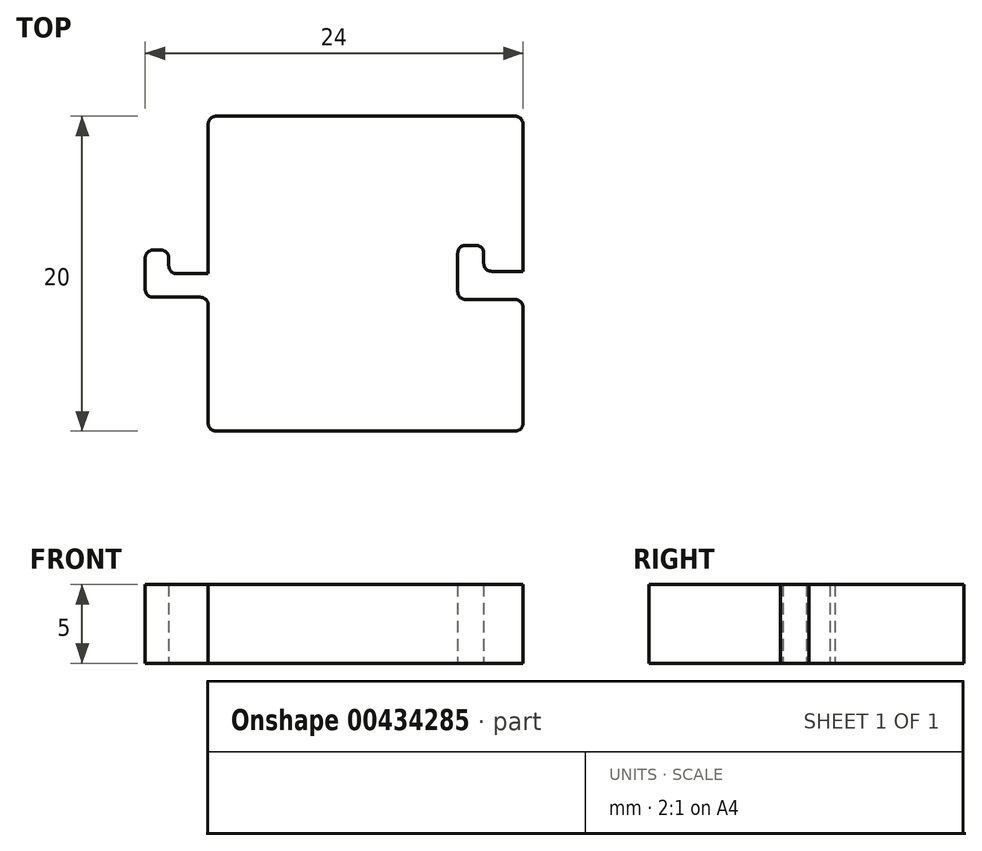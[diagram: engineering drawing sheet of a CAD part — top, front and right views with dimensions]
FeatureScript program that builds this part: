
annotation { "Feature Type Name" : "Feature", "Feature Type Description" : "" }
export const myFeature = defineFeature(function(context is Context, id is Id, definition is map)
    precondition{}
    {
        {
            var Q0;
            Q0=qCreatedBy(makeId("Top.planeOp"),FACE);
            var sketch = newSketch(context, id + "F0", { "sketchPlane" : qUnion([Q0])});
            skLineSegment(sketch, "E0.bottom", {"start": v(10, -10) * mm, "end": v(-10, -10) * mm});
            skLineSegment(sketch, "E0.top", {"start": v(10, 10) * mm, "end": v(-10, 10) * mm});
            skLineSegment(sketch, "E0.left", {"start": v(10, -10) * mm, "end": v(10, 10) * mm});
            skLineSegment(sketch, "E0.right", {"start": v(-10, -10) * mm, "end": v(-10, 10) * mm});
            skPoint(sketch, "E0.middle", {"position": v(0, 0) * mm});
            skSolve(sketch);
        }
        {
            var Q0;
            Q0 = qSketchRegion(id + "F0", true);
            extrude(context, id + "F1", {"entities" : qUnion([Q0]), "depth" : 5 * mm});
        }
        {
            var Q0;
            Q0=qCreatedBy(makeId("Top.planeOp"),FACE);
            var sketch = newSketch(context, id + "F2", { "sketchPlane" : qUnion([Q0])});
            skLineSegment(sketch, "E1.bottom", {"start": v(-10, 0) * mm, "end": v(-14, 0) * mm});
            skLineSegment(sketch, "E1.top", {"start": v(-10, -1.5) * mm, "end": v(-14, -1.5) * mm});
            skLineSegment(sketch, "E1.left", {"start": v(-10, 0) * mm, "end": v(-10, -1.5) * mm});
            skLineSegment(sketch, "E1.right", {"start": v(-14, 0) * mm, "end": v(-14, -1.5) * mm});
            skLineSegment(sketch, "E2.bottom", {"start": v(-14, 0) * mm, "end": v(-12.5, 0) * mm});
            skLineSegment(sketch, "E2.top", {"start": v(-14, 1.5) * mm, "end": v(-12.5, 1.5) * mm});
            skLineSegment(sketch, "E2.left", {"start": v(-14, 0) * mm, "end": v(-14, 1.5) * mm});
            skLineSegment(sketch, "E2.right", {"start": v(-12.5, 0) * mm, "end": v(-12.5, 1.5) * mm});
            skSolve(sketch);
        }
        {
            var Q0;
            Q0 = qSketchRegion(id + "F2", true);
            extrude(context, id + "F3", {"entities" : qUnion([Q0]), "operationType" : NewBodyOperationType.ADD, "depth" : 5 * mm});
        }
        {
            var Q0;
            Q0=qCreatedBy(makeId("Top.planeOp"),FACE);
            var sketch = newSketch(context, id + "F4", { "sketchPlane" : qUnion([Q0])});
            skLineSegment(sketch, "E3.bottom", {"start": v(10, 0.15) * mm, "end": v(5.85, 0.15) * mm});
            skLineSegment(sketch, "E3.top", {"start": v(10, -1.65) * mm, "end": v(5.85, -1.65) * mm});
            skLineSegment(sketch, "E3.left", {"start": v(10, 0.15) * mm, "end": v(10, -1.65) * mm});
            skLineSegment(sketch, "E3.right", {"start": v(5.85, 0.15) * mm, "end": v(5.85, -1.65) * mm});
            skLineSegment(sketch, "E4.bottom", {"start": v(5.85, 0.15) * mm, "end": v(7.5, 0.15) * mm});
            skLineSegment(sketch, "E4.top", {"start": v(5.85, 1.8) * mm, "end": v(7.5, 1.8) * mm});
            skLineSegment(sketch, "E4.left", {"start": v(5.85, 0.15) * mm, "end": v(5.85, 1.8) * mm});
            skLineSegment(sketch, "E4.right", {"start": v(7.5, 0.15) * mm, "end": v(7.5, 1.8) * mm});
            skSolve(sketch);
        }
        {
            var Q0;
            Q0 = qSketchRegion(id + "F4", true);
            extrude(context, id + "F5", {"entities" : qUnion([Q0]), "operationType" : NewBodyOperationType.REMOVE, "depth" : 5 * mm});
        }
        {
            var Q0;
            Q0=makeQuery(id+"F3.opExtrude","SWEPT_EDGE",EDGE,{"disambiguationData":[OSD([sQuery(id+"F2.wireOp",EDGE,"E1.top"),sQuery(id+"F2.wireOp",EDGE,"E1.right")])]});
            var Q1;
            Q1=makeQuery(id+"F3.opExtrude","SWEPT_EDGE",EDGE,{"disambiguationData":[OSD([sQuery(id+"F2.wireOp",EDGE,"E2.top"),sQuery(id+"F2.wireOp",EDGE,"E2.left")])]});
            var Q2;
            Q2=makeQuery(id+"F3.opExtrude","SWEPT_EDGE",EDGE,{"disambiguationData":[OSD([sQuery(id+"F2.wireOp",EDGE,"E2.top"),sQuery(id+"F2.wireOp",EDGE,"E2.right")])]});
            var Q3;
            Q3=makeQuery(id+"F3.opExtrude","SWEPT_EDGE",EDGE,{"disambiguationData":[OSD([sQuery(id+"F2.wireOp",EDGE,"E1.bottom"),sQuery(id+"F2.wireOp",EDGE,"E1.left")])]});
            var Q4;
            Q4=makeQuery(id+"F3.opExtrude","SWEPT_EDGE",EDGE,{"disambiguationData":[OSD([sQuery(id+"F2.wireOp",EDGE,"E1.bottom"),sQuery(id+"F2.wireOp",EDGE,"E2.bottom"),sQuery(id+"F2.wireOp",EDGE,"E2.right")])]});
            var Q5;
            Q5=makeQuery(id+"F3.opExtrude","SWEPT_EDGE",EDGE,{"disambiguationData":[OSD([sQuery(id+"F2.wireOp",EDGE,"E1.top"),sQuery(id+"F2.wireOp",EDGE,"E1.left")])]});
            var Q6;
            Q6=makeQuery(id+"F5.boolean.opBoolean","COPY",EDGE,{"derivedFrom":makeQuery(id+"F5.opExtrude","SWEPT_EDGE",EDGE,{"disambiguationData":[OSD([sQuery(id+"F4.wireOp",EDGE,"E4.top"),sQuery(id+"F4.wireOp",EDGE,"E4.left")])]})});
            var Q7;
            Q7=makeQuery(id+"F5.boolean.opBoolean","COPY",EDGE,{"derivedFrom":makeQuery(id+"F5.opExtrude","SWEPT_EDGE",EDGE,{"disambiguationData":[OSD([sQuery(id+"F4.wireOp",EDGE,"E4.top"),sQuery(id+"F4.wireOp",EDGE,"E4.right")])]})});
            var Q8;
            Q8=makeQuery(id+"F5.boolean.opBoolean","COPY",EDGE,{"derivedFrom":makeQuery(id+"F5.opExtrude","SWEPT_EDGE",EDGE,{"disambiguationData":[OSD([sQuery(id+"F4.wireOp",EDGE,"E3.bottom"),sQuery(id+"F4.wireOp",EDGE,"E4.bottom"),sQuery(id+"F4.wireOp",EDGE,"E4.right")])]})});
            var Q9;
            Q9=makeQuery(id+"F5.boolean.opBoolean","COPY",EDGE,{"derivedFrom":makeQuery(id+"F5.opExtrude","SWEPT_EDGE",EDGE,{"disambiguationData":[OSD([sQuery(id+"F4.wireOp",EDGE,"E3.bottom"),sQuery(id+"F4.wireOp",EDGE,"E3.left")])]})});
            var Q10;
            Q10=makeQuery(id+"F5.boolean.opBoolean","COPY",EDGE,{"derivedFrom":makeQuery(id+"F5.opExtrude","SWEPT_EDGE",EDGE,{"disambiguationData":[OSD([sQuery(id+"F4.wireOp",EDGE,"E3.top"),sQuery(id+"F4.wireOp",EDGE,"E3.left")])]})});
            var Q11;
            Q11=makeQuery(id+"F5.boolean.opBoolean","COPY",EDGE,{"derivedFrom":makeQuery(id+"F5.opExtrude","SWEPT_EDGE",EDGE,{"disambiguationData":[OSD([sQuery(id+"F4.wireOp",EDGE,"E3.top"),sQuery(id+"F4.wireOp",EDGE,"E3.right")])]})});
            var Q12;
            Q12=makeQuery(id+"F1.opExtrude","SWEPT_EDGE",EDGE,{"disambiguationData":[OSD([sQuery(id+"F0.wireOp",EDGE,"E0.bottom"),sQuery(id+"F0.wireOp",EDGE,"E0.left")])]});
            var Q13;
            Q13=makeQuery(id+"F1.opExtrude","SWEPT_EDGE",EDGE,{"disambiguationData":[OSD([sQuery(id+"F0.wireOp",EDGE,"E0.top"),sQuery(id+"F0.wireOp",EDGE,"E0.left")])]});
            var Q14;
            Q14=makeQuery(id+"F1.opExtrude","SWEPT_EDGE",EDGE,{"disambiguationData":[OSD([sQuery(id+"F0.wireOp",EDGE,"E0.top"),sQuery(id+"F0.wireOp",EDGE,"E0.right")])]});
            var Q15;
            Q15=makeQuery(id+"F1.opExtrude","SWEPT_EDGE",EDGE,{"disambiguationData":[OSD([sQuery(id+"F0.wireOp",EDGE,"E0.bottom"),sQuery(id+"F0.wireOp",EDGE,"E0.right")])]});
            fillet(context, id + "F6", {"entities" : qUnion([Q0, Q1, Q2, Q3, Q4, Q5, Q6, Q7, Q8, Q9, Q10, Q11, Q12, Q13, Q14, Q15]), "radius" : 0.5 * mm, "tangentPropagation" : true, "allowEdgeOverflow" : false});
        }
    });
